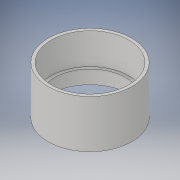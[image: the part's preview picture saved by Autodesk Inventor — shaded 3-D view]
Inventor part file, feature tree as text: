
AUTODESK INVENTOR PART (.ipt)
format: ipt  version: 2017 (Build 210142000, 142)  size: 110,592 bytes
history: native  units: in
note: dims shown in document units (in); Inventor stores cm internally (conversion verified against a paired STEP export)
features: revolve x1, sketch x1
ambient origin geometry x8: Origin, YZ Plane, XZ Plane, XY Plane, X Axis, Y Axis, Z Axis, Center Point
bodies: Solid1 (feature_tree)
feature tree (2):
  revolve  "Revolution1"  [1 undecoded]
  sketch  "Sketch1"  dims[d0=0.25in d1=0.125in d2=105.0deg d3=3.0in d4=0.25in d5=90.0deg d6=4.0in]
note: 1 required parameter value undecoded (feature->parameter linkage not recoverable at this tier; creation-order binding heuristic only, values carry confidence <= 0.55)
